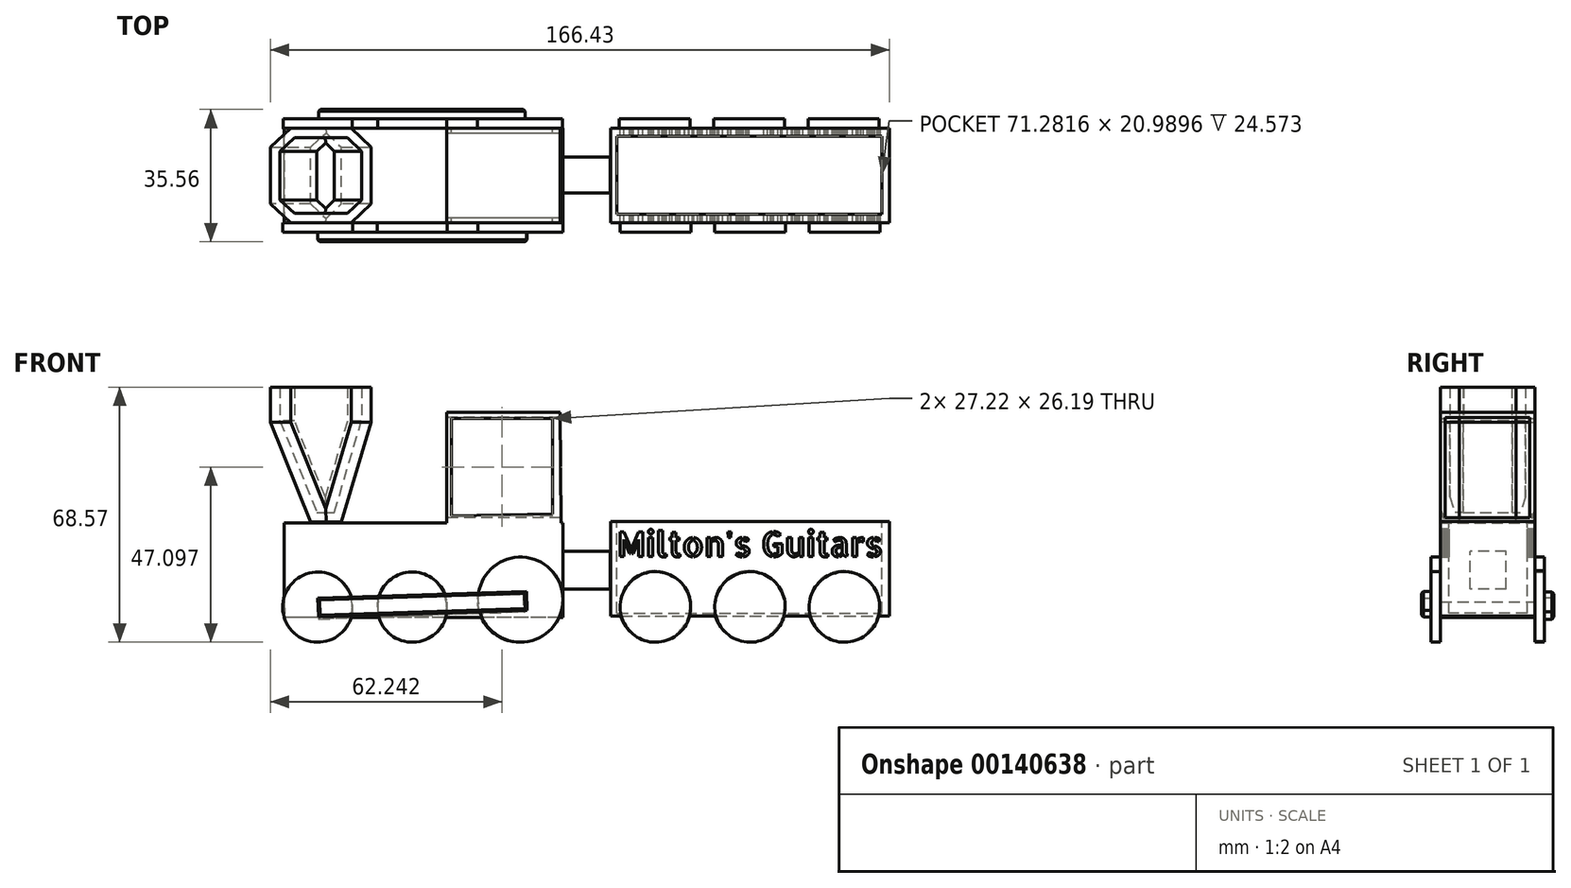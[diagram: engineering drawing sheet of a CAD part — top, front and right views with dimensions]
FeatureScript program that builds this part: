
annotation { "Feature Type Name" : "Feature", "Feature Type Description" : "" }
export const myFeature = defineFeature(function(context is Context, id is Id, definition is map)
    precondition{}
    {
        {
            var Q0;
            Q0=qCreatedBy(makeId("Front.planeOp"),FACE);
            var sketch = newSketch(context, id + "F0", { "sketchPlane" : qUnion([Q0])});
            skLineSegment(sketch, "E0", {"start": v(-53.46, 2.41) * mm, "end": v(-53.46, -18.78) * mm});
            skLineSegment(sketch, "E1", {"start": v(-53.46, 2.41) * mm, "end": v(21.46, 2.41) * mm});
            skLineSegment(sketch, "E2", {"start": v(21.46, 2.41) * mm, "end": v(21.46, -22.99) * mm});
            skLineSegment(sketch, "E3", {"start": v(21.46, -22.99) * mm, "end": v(-53.28, -22.99) * mm});
            skLineSegment(sketch, "E4", {"start": v(-53.46, -18.78) * mm, "end": v(-53.28, -22.99) * mm});
            skSolve(sketch);
        }
        {
            var Q0;
            Q0 = qSketchRegion(id + "F0", true);
            extrude(context, id + "F1", {"entities" : qUnion([Q0]), "depth" : 25.4 * mm});
        }
        {
            var Q0;
            Q0=qCreatedBy(makeId("Front.planeOp"),FACE);
            var sketch = newSketch(context, id + "F2", { "sketchPlane" : qUnion([Q0])});
            skLineSegment(sketch, "E5", {"start": v(-46.34, 2.7) * mm, "end": v(-57.15, 29.51) * mm});
            skLineSegment(sketch, "E6", {"start": v(-57.15, 29.51) * mm, "end": v(-30.13, 29.51) * mm});
            skLineSegment(sketch, "E7", {"start": v(-30.13, 29.51) * mm, "end": v(-38.03, 2.7) * mm});
            skLineSegment(sketch, "E8", {"start": v(-46.34, 2.7) * mm, "end": v(-38.03, 2.7) * mm});
            skSolve(sketch);
        }
        {
            var Q0;
            Q0=makeQuery(id+"F2.imprint","IMPRINT",FACE,{"disambiguationData":[TD([[makeQuery(id+"F2.imprint","IMPRINT",EDGE,{"derivedFrom":sQuery(id+"F2.wireOp",EDGE,"E5")}),-1.0]])]});
            extrude(context, id + "F3", {"entities" : qUnion([Q0]), "depth" : 25.4 * mm});
        }
        {
            var Q0;
            Q0=makeQuery(id+"F3.opExtrude","CAP_EDGE",EDGE,{"disambiguationData":[OSD([sQuery(id+"F2.wireOp",EDGE,"E7")])],"isStart":false});
            chamfer(context, id + "F4", {"entities" : qUnion([Q0]), "width" : 5.08 * mm, "tangentPropagation" : true});
        }
        {
            var Q0;
            Q0=makeQuery(id+"F3.opExtrude","CAP_EDGE",EDGE,{"disambiguationData":[OSD([sQuery(id+"F2.wireOp",EDGE,"E5")])],"isStart":false});
            chamfer(context, id + "F5", {"entities" : qUnion([Q0]), "width" : 5.08 * mm, "tangentPropagation" : true});
        }
        {
            var Q0;
            Q0=makeQuery(id+"F3.opExtrude","CAP_EDGE",EDGE,{"disambiguationData":[OSD([sQuery(id+"F2.wireOp",EDGE,"E5")])],"isStart":true});
            chamfer(context, id + "F6", {"entities" : qUnion([Q0]), "width" : 5.08 * mm, "tangentPropagation" : true});
        }
        {
            var Q0;
            Q0=makeQuery(id+"F3.opExtrude","CAP_EDGE",EDGE,{"disambiguationData":[OSD([sQuery(id+"F2.wireOp",EDGE,"E7")])],"isStart":true});
            chamfer(context, id + "F7", {"entities" : qUnion([Q0]), "width" : 5.08 * mm, "tangentPropagation" : true});
        }
        {
            var Q0;
            Q0=makeQuery(id+"F3.opExtrude","SWEPT_FACE",FACE,{"disambiguationData":[OSD([sQuery(id+"F2.wireOp",EDGE,"E6")])]});
            extrude(context, id + "F8", {"entities" : qUnion([Q0]), "operationType" : NewBodyOperationType.ADD, "depth" : 9.42 * mm});
        }
        {
            var Q0;
            Q0=makeQuery(id+"F8.opExtrude","CAP_FACE",FACE,{"disambiguationData":[OSD([sQuery(id+"F2.wireOp",EDGE,"E6")])],"isStart":false});
            shell(context, id + "F9", {"entities" : qUnion([Q0]), "thickness" : 2.54 * mm});
        }
        {
            var Q0;
            Q0=qCreatedBy(makeId("Front.planeOp"),FACE);
            var sketch = newSketch(context, id + "F10", { "sketchPlane" : qUnion([Q0])});
            skLineSegment(sketch, "E9", {"start": v(20.95, 1.72) * mm, "end": v(-9.73, 1.72) * mm});
            skLineSegment(sketch, "E10", {"start": v(-9.73, 1.72) * mm, "end": v(-9.73, 32.2) * mm});
            skLineSegment(sketch, "E11", {"start": v(-9.73, 32.2) * mm, "end": v(20.75, 32.2) * mm});
            skLineSegment(sketch, "E12", {"start": v(20.75, 32.2) * mm, "end": v(20.95, 1.72) * mm});
            skSolve(sketch);
        }
        {
            var Q0;
            Q0=makeQuery(id+"F10.imprint","IMPRINT",FACE,{"disambiguationData":[TD([[makeQuery(id+"F10.imprint","IMPRINT",EDGE,{"derivedFrom":sQuery(id+"F10.wireOp",EDGE,"E9")}),-1.0]])]});
            extrude(context, id + "F11", {"entities" : qUnion([Q0]), "operationType" : NewBodyOperationType.ADD, "depth" : 25.4 * mm});
        }
        {
            var Q0;
            Q0=qCreatedBy(makeId("Front.planeOp"),FACE);
            var sketch = newSketch(context, id + "F12", { "sketchPlane" : qUnion([Q0])});
            skLineSegment(sketch, "E13", {"start": v(-8.52, 30.55) * mm, "end": v(-8.52, 4.36) * mm});
            skLineSegment(sketch, "E14", {"start": v(-8.52, 30.55) * mm, "end": v(18.7, 30.55) * mm});
            skLineSegment(sketch, "E15", {"start": v(18.7, 30.55) * mm, "end": v(18.7, 4.78) * mm});
            skLineSegment(sketch, "E16", {"start": v(-8.52, 4.36) * mm, "end": v(18.7, 4.78) * mm});
            skSolve(sketch);
        }
        {
            var Q0;
            Q0=makeQuery(id+"F12.imprint","IMPRINT",FACE,{"disambiguationData":[TD([[makeQuery(id+"F12.imprint","IMPRINT",EDGE,{"derivedFrom":sQuery(id+"F12.wireOp",EDGE,"E13")}),1.0]])]});
            extrude(context, id + "F13", {"entities" : qUnion([Q0]), "operationType" : NewBodyOperationType.REMOVE, "depth" : 30.08 * mm});
        }
        {
            var Q0;
            Q0=makeQuery(id+"F11.opExtrude","SWEPT_FACE",FACE,{"disambiguationData":[OSD([sQuery(id+"F10.wireOp",EDGE,"E10")])]});
            var sketch = newSketch(context, id + "F14", { "sketchPlane" : qUnion([Q0])});
            skLineSegment(sketch, "E17.bottom", {"start": v(1.33, 30.72) * mm, "end": v(24.06, 30.72) * mm});
            skLineSegment(sketch, "E17.top", {"start": v(1.33, 3.83) * mm, "end": v(24.06, 3.83) * mm});
            skLineSegment(sketch, "E17.left", {"start": v(1.33, 30.72) * mm, "end": v(1.33, 3.83) * mm});
            skLineSegment(sketch, "E17.right", {"start": v(24.06, 30.72) * mm, "end": v(24.06, 3.83) * mm});
            skSolve(sketch);
        }
        {
            var Q0;
            Q0=makeQuery(id+"F14.imprint","IMPRINT",FACE,{"disambiguationData":[TD([[makeQuery(id+"F14.imprint","IMPRINT",EDGE,{"derivedFrom":sQuery(id+"F14.wireOp",EDGE,"E17.bottom")}),-1.0]])]});
            extrude(context, id + "F15", {"entities" : qUnion([Q0]), "operationType" : NewBodyOperationType.REMOVE, "oppositeDirection" : true, "depth" : 34.25 * mm});
        }
        {
            var Q0;
            Q0=qCreatedBy(makeId("Front.planeOp"),FACE);
            var sketch = newSketch(context, id + "F16", { "sketchPlane" : qUnion([Q0])});
            skCircle(sketch, "E18", {"center": v(-44.45, -20.2) * mm, "radius": 9.3 * mm});
            skCircle(sketch, "E19.1.0.0", {"center": v(-19.05, -20.2) * mm, "radius": 9.3 * mm});
            skLineSegment(sketch, "E19.direction1", {"start": v(-44.45, -20.2) * mm, "end": v(-19.05, -20.2) * mm, "construction": true});
            skCircle(sketch, "E20", {"center": v(9.9, -18.18) * mm, "radius": 11.43 * mm});
            skSolve(sketch);
        }
        {
            var Q0;
            Q0=makeQuery(id+"F16.imprint","IMPRINT",FACE,{"disambiguationData":[TD([[makeQuery(id+"F16.imprint","IMPRINT",EDGE,{"derivedFrom":sQuery(id+"F16.wireOp",EDGE,"E19.1.0.0")}),1.0]])]});
            var Q1;
            Q1=sQuery(id+"F16.wireOp",EDGE,"E19.1.0.0");
            extrude(context, id + "F17", {"entities" : qUnion([Q0]), "surfaceEntities" : qUnion([Q1]), "oppositeDirection" : true, "depth" : 2.54 * mm});
        }
        {
            var Q0;
            Q0 = qSketchRegion(id + "F16", true);
            extrude(context, id + "F18", {"entities" : qUnion([Q0]), "oppositeDirection" : true, "depth" : 2.54 * mm});
        }
        {
            var Q0;
            Q0=makeQuery(id+"F11.boolean.opBoolean","MERGE",FACE,{"derivedFrom":[makeQuery(id+"F1.opExtrude","CAP_FACE",FACE,{"disambiguationData":[OSD([sQuery(id+"F0.wireOp",EDGE,"E0"),sQuery(id+"F0.wireOp",EDGE,"E1"),sQuery(id+"F0.wireOp",EDGE,"E2"),sQuery(id+"F0.wireOp",EDGE,"E3"),sQuery(id+"F0.wireOp",EDGE,"E4")])],"isStart":false}),makeQuery(id+"F11.opExtrude","CAP_FACE",FACE,{"disambiguationData":[OSD([sQuery(id+"F10.wireOp",EDGE,"E9"),sQuery(id+"F10.wireOp",EDGE,"E10"),sQuery(id+"F10.wireOp",EDGE,"E11"),sQuery(id+"F10.wireOp",EDGE,"E12")])],"isStart":false})]});
            var sketch = newSketch(context, id + "F19", { "sketchPlane" : qUnion([Q0])});
            skCircle(sketch, "E21", {"center": v(10.1, -18.18) * mm, "radius": 11.43 * mm});
            skCircle(sketch, "E22", {"center": v(-19, -20.2) * mm, "radius": 9.42 * mm});
            skCircle(sketch, "E23.1.0.0", {"center": v(-44.4, -20.2) * mm, "radius": 9.42 * mm});
            skLineSegment(sketch, "E23.direction1", {"start": v(-19, -20.2) * mm, "end": v(-44.4, -20.2) * mm, "construction": true});
            skSolve(sketch);
        }
        {
            var Q0;
            Q0 = qSketchRegion(id + "F19", true);
            extrude(context, id + "F20", {"entities" : qUnion([Q0]), "operationType" : NewBodyOperationType.ADD, "depth" : 2.54 * mm});
        }
        {
            var Q0;
            Q0=makeQuery(id+"F1.opExtrude","SWEPT_FACE",FACE,{"disambiguationData":[OSD([sQuery(id+"F0.wireOp",EDGE,"E2")])]});
            var sketch = newSketch(context, id + "F21", { "sketchPlane" : qUnion([Q0])});
            skLineSegment(sketch, "E24.bottom", {"start": v(-7.68, -15.36) * mm, "end": v(-17.38, -15.36) * mm});
            skLineSegment(sketch, "E24.top", {"start": v(-7.68, -5.22) * mm, "end": v(-17.38, -5.22) * mm});
            skLineSegment(sketch, "E24.left", {"start": v(-7.68, -15.36) * mm, "end": v(-7.68, -5.22) * mm});
            skLineSegment(sketch, "E24.right", {"start": v(-17.38, -15.36) * mm, "end": v(-17.38, -5.22) * mm});
            skPoint(sketch, "E24.middle", {"position": v(-12.53, -10.29) * mm});
            skPoint(sketch, "E24.middle.positionSnap0", {"position": v(0, -10.29) * mm});
            skPoint(sketch, "E24.centerSnap0", {"position": v(0, -10.29) * mm});
            skSolve(sketch);
        }
        {
            var Q0;
            Q0=makeQuery(id+"F21.imprint","IMPRINT",FACE,{"disambiguationData":[TD([[makeQuery(id+"F21.imprint","IMPRINT",EDGE,{"derivedFrom":sQuery(id+"F21.wireOp",EDGE,"E24.bottom")}),-1.0]])]});
            extrude(context, id + "F22", {"entities" : qUnion([Q0]), "operationType" : NewBodyOperationType.ADD, "depth" : 12.7 * mm});
        }
        {
            var Q0;
            Q0=qCreatedBy(makeId("Front.planeOp"),FACE);
            var sketch = newSketch(context, id + "F23", { "sketchPlane" : qUnion([Q0])});
            skLineSegment(sketch, "E25.bottom", {"start": v(34.35, 2.74) * mm, "end": v(109.28, 2.74) * mm});
            skLineSegment(sketch, "E25.top", {"start": v(34.35, -22.66) * mm, "end": v(109.28, -22.66) * mm});
            skLineSegment(sketch, "E25.left", {"start": v(34.35, 2.74) * mm, "end": v(34.35, -22.66) * mm});
            skLineSegment(sketch, "E25.right", {"start": v(109.28, 2.74) * mm, "end": v(109.28, -22.66) * mm});
            skText(sketch, "E26", { "text": "Milton\'s Guitars", "fontName": "AllertaStencil-Regular.ttf"});
            const initialGuessF23  = {"E26": [0.03597, -0.00665, 1, 0, 0.00665]};
            skSetInitialGuess(sketch, initialGuessF23);
            skSolve(sketch);
        }
        {
            var Q0;
            Q0=makeQuery(id+"F23.imprint","IMPRINT",FACE,{"disambiguationData":[TD([[makeQuery(id+"F23.imprint","IMPRINT",EDGE,{"derivedFrom":sQuery(id+"F23.wireOp",EDGE,"E25.bottom")}),-1.0]])]});
            extrude(context, id + "F24", {"entities" : qUnion([Q0]), "depth" : 25.4 * mm});
        }
        {
            var Q0;
            Q0=makeQuery(id+"F24.opExtrude","CAP_FACE",FACE,{"disambiguationData":[OSD([sQuery(id+"F23.wireOp",EDGE,"E25.bottom"),sQuery(id+"F23.wireOp",EDGE,"E25.top"),sQuery(id+"F23.wireOp",EDGE,"E25.left"),sQuery(id+"F23.wireOp",EDGE,"E25.right")])],"isStart":false});
            var sketch = newSketch(context, id + "F25", { "sketchPlane" : qUnion([Q0])});
            skCircle(sketch, "E27", {"center": v(46.36, -20.16) * mm, "radius": 9.48 * mm});
            skCircle(sketch, "E28.1.0.0", {"center": v(71.76, -20.16) * mm, "radius": 9.48 * mm});
            skCircle(sketch, "E28.2.0.0", {"center": v(97.16, -20.16) * mm, "radius": 9.48 * mm});
            skLineSegment(sketch, "E28.direction1", {"start": v(46.36, -20.16) * mm, "end": v(71.76, -20.16) * mm, "construction": true});
            skSolve(sketch);
        }
        {
            var Q0;
            Q0 = qSketchRegion(id + "F25", true);
            extrude(context, id + "F26", {"entities" : qUnion([Q0]), "operationType" : NewBodyOperationType.ADD, "depth" : 2.54 * mm});
        }
        {
            var Q0;
            Q0=makeQuery(id+"F24.opExtrude","CAP_FACE",FACE,{"disambiguationData":[OSD([sQuery(id+"F23.wireOp",EDGE,"E25.bottom"),sQuery(id+"F23.wireOp",EDGE,"E25.top"),sQuery(id+"F23.wireOp",EDGE,"E25.left"),sQuery(id+"F23.wireOp",EDGE,"E25.right")])],"isStart":true});
            var sketch = newSketch(context, id + "F27", { "sketchPlane" : qUnion([Q0])});
            skCircle(sketch, "E29", {"center": v(-46.15, -19.95) * mm, "radius": 9.49 * mm});
            skCircle(sketch, "E30.1.0.0", {"center": v(-71.55, -19.95) * mm, "radius": 9.49 * mm});
            skCircle(sketch, "E30.2.0.0", {"center": v(-96.95, -19.95) * mm, "radius": 9.49 * mm});
            skLineSegment(sketch, "E30.direction1", {"start": v(-46.15, -19.95) * mm, "end": v(-71.55, -19.95) * mm, "construction": true});
            skSolve(sketch);
        }
        {
            var Q0;
            Q0 = qSketchRegion(id + "F27", true);
            extrude(context, id + "F28", {"entities" : qUnion([Q0]), "operationType" : NewBodyOperationType.ADD, "depth" : 2.54 * mm});
        }
        {
            var Q0;
            Q0=makeQuery(id+"F24.opExtrude","SWEPT_FACE",FACE,{"disambiguationData":[OSD([sQuery(id+"F23.wireOp",EDGE,"E25.bottom")])]});
            var sketch = newSketch(context, id + "F29", { "sketchPlane" : qUnion([Q0])});
            skLineSegment(sketch, "E31.bottom", {"start": v(35.97, -2.08) * mm, "end": v(107.25, -2.08) * mm});
            skLineSegment(sketch, "E31.top", {"start": v(35.97, -23.07) * mm, "end": v(107.25, -23.07) * mm});
            skLineSegment(sketch, "E31.left", {"start": v(35.97, -2.08) * mm, "end": v(35.97, -23.07) * mm});
            skLineSegment(sketch, "E31.right", {"start": v(107.25, -2.08) * mm, "end": v(107.25, -23.07) * mm});
            skSolve(sketch);
        }
        {
            var Q0;
            Q0=makeQuery(id+"F29.imprint","IMPRINT",FACE,{"disambiguationData":[TD([[makeQuery(id+"F29.imprint","IMPRINT",EDGE,{"derivedFrom":sQuery(id+"F29.wireOp",EDGE,"E31.bottom")}),-1.0]])]});
            extrude(context, id + "F30", {"entities" : qUnion([Q0]), "operationType" : NewBodyOperationType.REMOVE, "oppositeDirection" : true, "depth" : 24.57 * mm});
        }
        {
            var Q0;
            Q0=makeQuery(id+"F20.opExtrude","CAP_FACE",FACE,{"disambiguationData":[OSD([sQuery(id+"F19.wireOp",EDGE,"E23.1.0.0")])],"isStart":false});
            var sketch = newSketch(context, id + "F31", { "sketchPlane" : qUnion([Q0])});
            skLineSegment(sketch, "E32", {"start": v(-44.4, -17.76) * mm, "end": v(-44.23, -22.83) * mm});
            skLineSegment(sketch, "E33", {"start": v(-44.4, -17.76) * mm, "end": v(11.65, -16) * mm});
            skLineSegment(sketch, "E34", {"start": v(-44.23, -22.83) * mm, "end": v(11.87, -21.08) * mm});
            skLineSegment(sketch, "E35", {"start": v(11.65, -16) * mm, "end": v(11.87, -21.08) * mm});
            skSolve(sketch);
        }
        {
            var Q0;
            Q0 = qSketchRegion(id + "F31", true);
            extrude(context, id + "F32", {"entities" : qUnion([Q0]), "operationType" : NewBodyOperationType.ADD, "depth" : 2.54 * mm});
        }
        {
            var Q0;
            Q0=makeQuery(id+"F32.opExtrude","CAP_EDGE",EDGE,{"disambiguationData":[OSD([sQuery(id+"F31.wireOp",EDGE,"E33")])],"isStart":false});
            chamfer(context, id + "F33", {"entities" : qUnion([Q0]), "width" : 0.5 * mm, "tangentPropagation" : true});
        }
        {
            var Q0;
            Q0=makeQuery(id+"F32.opExtrude","CAP_EDGE",EDGE,{"disambiguationData":[OSD([sQuery(id+"F31.wireOp",EDGE,"E34")])],"isStart":false});
            chamfer(context, id + "F34", {"entities" : qUnion([Q0]), "width" : 0.5 * mm, "tangentPropagation" : true});
        }
        {
            var Q0;
            Q0=makeQuery(id+"F32.opExtrude","CAP_EDGE",EDGE,{"disambiguationData":[OSD([sQuery(id+"F31.wireOp",EDGE,"E32")])],"isStart":false});
            var Q1;
            Q1=makeQuery(id+"F32.opExtrude","CAP_EDGE",EDGE,{"disambiguationData":[OSD([sQuery(id+"F31.wireOp",EDGE,"E35")])],"isStart":false});
            chamfer(context, id + "F35", {"entities" : qUnion([Q0, Q1]), "width" : 0.5 * mm, "tangentPropagation" : true});
        }
        {
            var Q0;
            Q0=makeQuery(id+"F17.opExtrude","CAP_FACE",FACE,{"disambiguationData":[OSD([sQuery(id+"F16.wireOp",EDGE,"E19.1.0.0")])],"isStart":false});
            var sketch = newSketch(context, id + "F36", { "sketchPlane" : qUnion([Q0])});
            skLineSegment(sketch, "E36", {"start": v(-11.39, -16.16) * mm, "end": v(-11.39, -21.42) * mm});
            skLineSegment(sketch, "E37", {"start": v(-11.39, -21.42) * mm, "end": v(44.18, -23.44) * mm});
            skLineSegment(sketch, "E38", {"start": v(44.18, -23.44) * mm, "end": v(44.18, -17.78) * mm});
            skLineSegment(sketch, "E39", {"start": v(44.18, -17.78) * mm, "end": v(-11.39, -16.16) * mm});
            skSolve(sketch);
        }
        {
            var Q0;
            Q0 = qSketchRegion(id + "F36", true);
            extrude(context, id + "F37", {"entities" : qUnion([Q0]), "depth" : 2.54 * mm});
        }
        {
            var Q0;
            Q0=makeQuery(id+"F37.opExtrude","CAP_EDGE",EDGE,{"disambiguationData":[OSD([sQuery(id+"F36.wireOp",EDGE,"E39")])],"isStart":false});
            var Q1;
            Q1=makeQuery(id+"F37.opExtrude","CAP_EDGE",EDGE,{"disambiguationData":[OSD([sQuery(id+"F36.wireOp",EDGE,"E38")])],"isStart":false});
            var Q2;
            Q2=makeQuery(id+"F37.opExtrude","CAP_EDGE",EDGE,{"disambiguationData":[OSD([sQuery(id+"F36.wireOp",EDGE,"E37")])],"isStart":false});
            var Q3;
            Q3=makeQuery(id+"F37.opExtrude","CAP_EDGE",EDGE,{"disambiguationData":[OSD([sQuery(id+"F36.wireOp",EDGE,"E36")])],"isStart":false});
            chamfer(context, id + "F38", {"entities" : qUnion([Q0, Q1, Q2, Q3]), "width" : 0.5 * mm, "tangentPropagation" : true});
        }
    });
